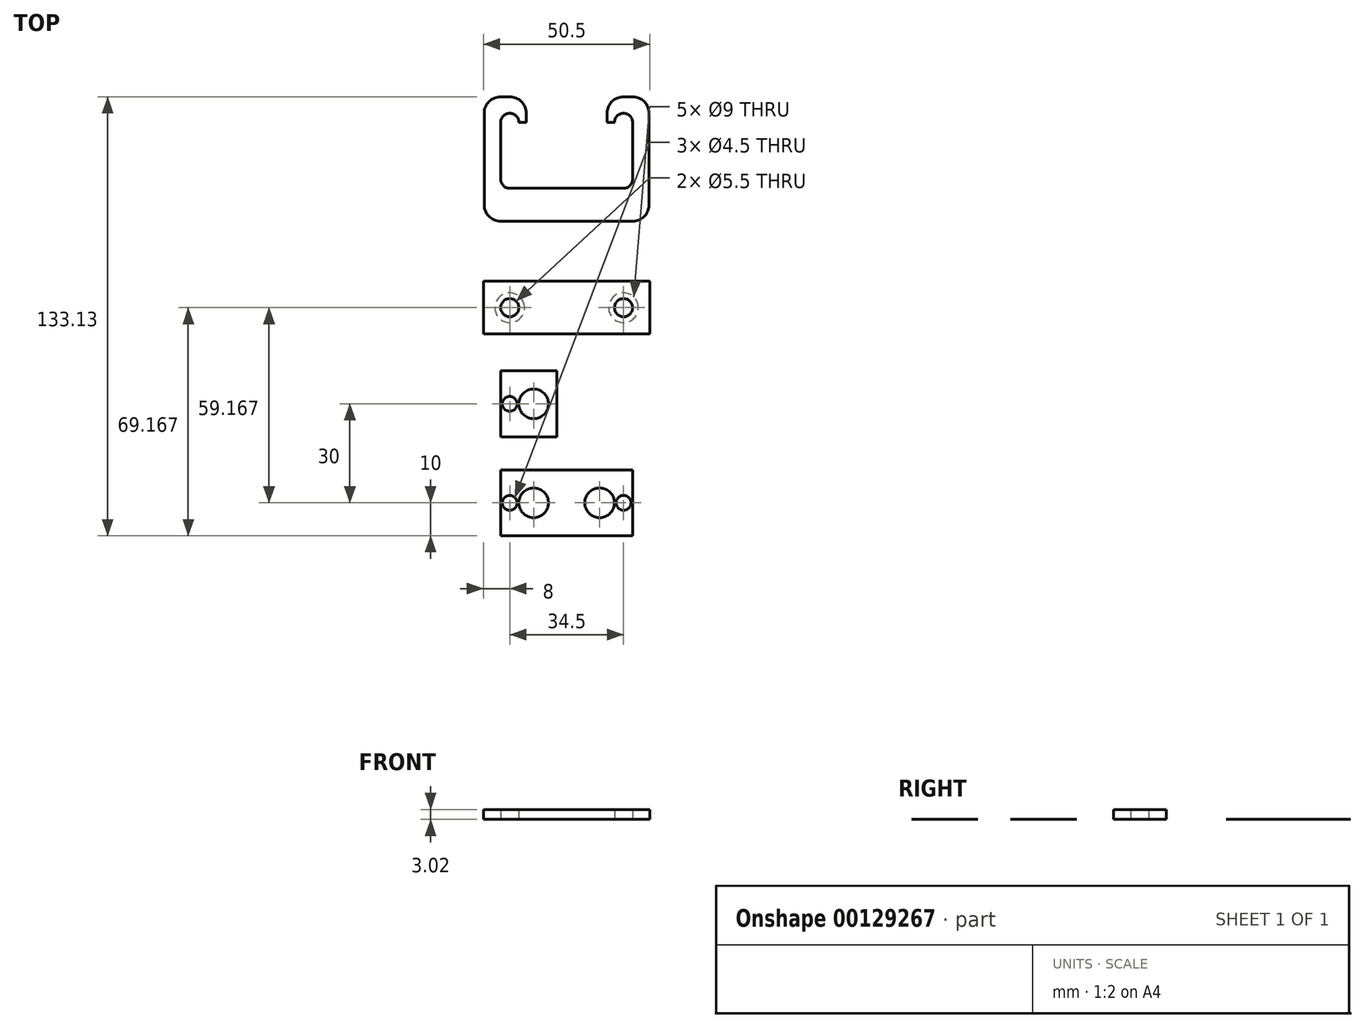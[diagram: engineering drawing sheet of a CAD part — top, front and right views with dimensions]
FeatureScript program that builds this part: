
annotation { "Feature Type Name" : "Feature", "Feature Type Description" : "" }
export const myFeature = defineFeature(function(context is Context, id is Id, definition is map)
    precondition{}
    {
        {
            var Q0;
            Q0=qCreatedBy(makeId("Top.planeOp"),FACE);
            var sketch = newSketch(context, id + "F0", { "sketchPlane" : qUnion([Q0])});
            skLineSegment(sketch, "E0.bottom", {"start": v(20, -10) * mm, "end": v(-20, -10) * mm});
            skLineSegment(sketch, "E0.top", {"start": v(20, 10) * mm, "end": v(-20, 10) * mm});
            skLineSegment(sketch, "E0.left", {"start": v(20, -10) * mm, "end": v(20, 10) * mm});
            skLineSegment(sketch, "E0.right", {"start": v(-20, -10) * mm, "end": v(-20, 10) * mm});
            skPoint(sketch, "E0.middle", {"position": v(0, 0) * mm});
            skPoint(sketch, "E1", {"position": v(-10, 0) * mm});
            skPoint(sketch, "E2", {"position": v(10, 0) * mm});
            skCircle(sketch, "E3", {"center": v(-10, 0) * mm, "radius": 2.75 * mm});
            skCircle(sketch, "E4", {"center": v(-10, 0) * mm, "radius": 4.5 * mm});
            skPoint(sketch, "E5", {"position": v(-17.25, 0) * mm});
            skCircle(sketch, "E6", {"center": v(-17.25, 0) * mm, "radius": 2.25 * mm});
            skPoint(sketch, "E7", {"position": v(-14.5, 0) * mm});
            skLineSegment(sketch, "E8", {"start": v(-14.5, 0) * mm, "end": v(-20, 0) * mm, "construction": true});
            skPoint(sketch, "E9.MirrorP", {"position": v(17.25, 0) * mm});
            skCircle(sketch, "E10.MirrorC", {"center": v(10, 0) * mm, "radius": 4.5 * mm});
            skPoint(sketch, "E11.MirrorP", {"position": v(14.5, 0) * mm});
            skCircle(sketch, "E12.MirrorC", {"center": v(10, 0) * mm, "radius": 2.75 * mm});
            skCircle(sketch, "E13.MirrorC", {"center": v(17.25, 0) * mm, "radius": 2.25 * mm});
            skLineSegment(sketch, "E14.MirrorCS", {"start": v(14.5, 0) * mm, "end": v(20, 0) * mm, "construction": true});
            skLineSegment(sketch, "E15", {"start": v(-3, 10) * mm, "end": v(-3, -10) * mm});
            skLineSegment(sketch, "E16", {"start": v(3, -10) * mm, "end": v(3, 10) * mm});
            skLineSegment(sketch, "E17", {"start": v(0, 10) * mm, "end": v(0, -10) * mm});
            skSolve(sketch);
        }
        {
            var Q0;
            {var subQ0=sQuery(id+"F0.wireOp",EDGE,"E0.right");Q0=makeQuery(id+"F0.imprint","IMPRINT",FACE,{"disambiguationData":[TD([[makeQuery(id+"F0.imprint","IMPRINT",EDGE,{"derivedFrom":subQ0}),-1.0]])]});}
            var Q1;
            {var subQ0=sQuery(id+"F0.wireOp",EDGE,"E15");Q1=makeQuery(id+"F0.imprint","IMPRINT",FACE,{"disambiguationData":[TD([[makeQuery(id+"F0.imprint","IMPRINT",EDGE,{"derivedFrom":subQ0}),1.0]])]});}
            var Q2;
            {var subQ0=sQuery(id+"F0.wireOp",EDGE,"E16");Q2=makeQuery(id+"F0.imprint","IMPRINT",FACE,{"disambiguationData":[TD([[makeQuery(id+"F0.imprint","IMPRINT",EDGE,{"derivedFrom":subQ0}),1.0]])]});}
            var Q3;
            {var subQ1=sQuery(id+"F0.wireOp",EDGE,"E0.left");Q3=makeQuery(id+"F0.imprint","IMPRINT",FACE,{"disambiguationData":[TD([[makeQuery(id+"F0.imprint","IMPRINT",EDGE,{"derivedFrom":subQ1}),1.0]])]});}
            var Q4;
            Q4=makeQuery(id+"F0.imprint","IMPRINT",FACE,{"disambiguationData":[TD([[makeQuery(id+"F0.imprint","IMPRINT",EDGE,{"derivedFrom":sQuery(id+"F0.wireOp",EDGE,"E3")}),-1.0]])]});
            var Q5;
            Q5=makeQuery(id+"F0.imprint","IMPRINT",FACE,{"disambiguationData":[TD([[makeQuery(id+"F0.imprint","IMPRINT",EDGE,{"derivedFrom":sQuery(id+"F0.wireOp",EDGE,"E10.MirrorC")}),-1.0]])]});
            extrude(context, id + "F1", {"entities" : qUnion([Q0, Q1, Q2, Q3, Q4, Q5]), "oppositeDirection" : true, "depth" : 1 / 50.8 * mm});
        }
        {
            var Q0;
            Q0=makeQuery(id+"F0.imprint","IMPRINT",FACE,{"disambiguationData":[TD([[makeQuery(id+"F0.imprint","IMPRINT",EDGE,{"derivedFrom":sQuery(id+"F0.wireOp",EDGE,"E3")}),-1.0]])]});
            var Q1;
            Q1=makeQuery(id+"F0.imprint","IMPRINT",FACE,{"disambiguationData":[TD([[makeQuery(id+"F0.imprint","IMPRINT",EDGE,{"derivedFrom":sQuery(id+"F0.wireOp",EDGE,"E10.MirrorC")}),-1.0]])]});
            extrude(context, id + "F2", {"entities" : qUnion([Q0, Q1]), "operationType" : NewBodyOperationType.REMOVE, "oppositeDirection" : true, "depth" : 6 * mm});
        }
        {
            var Q0;
            Q0=makeQuery(id+"F1.opExtrude","SWEPT_FACE",FACE,{"disambiguationData":[OSD([sQuery(id+"F0.wireOp",EDGE,"E0.bottom")])]});
            var sketch = newSketch(context, id + "F3", { "sketchPlane" : qUnion([Q0])});
            skPoint(sketch, "E18.0", {"position": v(-3, 0) * mm});
            skPoint(sketch, "E19.0", {"position": v(0, 0) * mm});
            skPoint(sketch, "E20.0", {"position": v(3, 0) * mm});
            skLineSegment(sketch, "E21", {"start": v(-3, 0) * mm, "end": v(0, 0) * mm});
            skLineSegment(sketch, "E22", {"start": v(0, 0) * mm, "end": v(3, 0) * mm});
            skLineSegment(sketch, "E23", {"start": v(-3, 0) * mm, "end": v(-3, -3) * mm});
            skLineSegment(sketch, "E24", {"start": v(-3, -3) * mm, "end": v(3, -3) * mm});
            skLineSegment(sketch, "E25", {"start": v(3, -3) * mm, "end": v(3, 0) * mm});
            skSolve(sketch);
        }
        {
            var Q0;
            Q0=makeQuery(id+"F3.imprint","IMPRINT",FACE,{"disambiguationData":[TD([[makeQuery(id+"F3.imprint","IMPRINT",EDGE,{"derivedFrom":sQuery(id+"F3.wireOp",EDGE,"E21")}),1.0]])]});
            var Q1;
            Q1=sQuery(id+"F3.wireOp",EDGE,"E24");
            extrude(context, id + "F4", {"entities" : qUnion([Q0]), "operationType" : NewBodyOperationType.REMOVE, "surfaceEntities" : qUnion([Q1]), "oppositeDirection" : true, "depth" : 25 * mm});
        }
        {
            var Q0;
            Q0=qCreatedBy(makeId("Top.planeOp"),FACE);
            var sketch = newSketch(context, id + "F5", { "sketchPlane" : qUnion([Q0])});
            skLineSegment(sketch, "E26.bottom", {"start": v(-25.25, 21.17) * mm, "end": v(25.25, 21.17) * mm});
            skLineSegment(sketch, "E26.top", {"start": v(-25.25, 37.17) * mm, "end": v(25.25, 37.17) * mm});
            skLineSegment(sketch, "E26.left", {"start": v(-25.25, 21.17) * mm, "end": v(-25.25, 37.17) * mm});
            skLineSegment(sketch, "E26.right", {"start": v(25.25, 21.17) * mm, "end": v(25.25, 37.17) * mm});
            skLineSegment(sketch, "E27", {"start": v(0, 21.17) * mm, "end": v(0, 10.09) * mm, "construction": true});
            skLineSegment(sketch, "E28", {"start": v(-17.25, 0) * mm, "end": v(-17.25, 37.17) * mm, "construction": true});
            skLineSegment(sketch, "E29", {"start": v(17.25, 0) * mm, "end": v(17.25, 37.17) * mm, "construction": true});
            skLineSegment(sketch, "E30", {"start": v(-25.25, 29.17) * mm, "end": v(25.25, 29.17) * mm, "construction": true});
            skPoint(sketch, "E31.0", {"position": v(-3, 10) * mm});
            skPoint(sketch, "E32.0", {"position": v(3, 10) * mm});
            skLineSegment(sketch, "E33", {"start": v(-3, 10) * mm, "end": v(-3, 37.17) * mm, "construction": true});
            skLineSegment(sketch, "E34", {"start": v(3, 37.17) * mm, "end": v(3, 10) * mm, "construction": true});
            skPoint(sketch, "E35", {"position": v(-3, 21.17) * mm});
            skPoint(sketch, "E36", {"position": v(3, 21.17) * mm});
            skPoint(sketch, "E37", {"position": v(-17.25, 29.17) * mm});
            skPoint(sketch, "E38", {"position": v(17.25, 29.17) * mm});
            skSolve(sketch);
        }
        {
            var Q0;
            Q0 = qSketchRegion(id + "F5", true);
            var Q1;
            Q1=makeQuery(id+"F5.imprint","IMPRINT",FACE,{"disambiguationData":[TD([[makeQuery(id+"F5.imprint","IMPRINT",EDGE,{"derivedFrom":sQuery(id+"F5.wireOp",EDGE,"ofzVHqzz-uNpf-kPzX-PyAA-OWdwubVH7mjJ")}),-1.0]])]});
            var Q2;
            Q2=makeQuery(id+"F5.imprint","IMPRINT",FACE,{"disambiguationData":[TD([[makeQuery(id+"F5.imprint","IMPRINT",EDGE,{"derivedFrom":sQuery(id+"F5.wireOp",EDGE,"o32WaDat-DvT3-jpnh-iwgM-FfQ55ZiCaMmG")}),-1.0]])]});
            extrude(context, id + "F6", {"entities" : qUnion([Q0, Q1, Q2]), "oppositeDirection" : true, "depth" : 1 / 50.8 * mm});
        }
        {
            var Q0;
            Q0=sQuery(id+"F5.wireOp",VERTEX,"E37");
            var Q1;
            Q1=sQuery(id+"F5.wireOp",VERTEX,"E38");
            var Q2;
            Q2=makeQuery(id+"F6.opExtrude","SWEPT_BODY",BODY,{"disambiguationData":[OSD([sQuery(id+"F5.wireOp",EDGE,"E26.bottom"),sQuery(id+"F5.wireOp",EDGE,"E26.top"),sQuery(id+"F5.wireOp",EDGE,"E26.left"),sQuery(id+"F5.wireOp",EDGE,"E26.right")])]});
            hole(context, id + "F7", {"style" : HoleStyle.C_BORE, "endStyle" : HoleEndStyle.THROUGH, "holeDiameter" : 5.5 * mm, "cBoreDiameter" : 9 * mm, "cBoreDepth" : 5 * mm, "startFromSketch" : true, "locations" : qUnion([Q0, Q1]), "scope" : qUnion([Q2]), "isTappedThrough" : true});
        }
        {
            var Q0;
            Q0=qCreatedBy(makeId("Top.planeOp"),FACE);
            var sketch = newSketch(context, id + "F8", { "sketchPlane" : qUnion([Q0])});
            skLineSegment(sketch, "E39.bottom", {"start": v(25, 55.38) * mm, "end": v(-25, 55.38) * mm});
            skLineSegment(sketch, "E39.top", {"start": v(25, 80.88) * mm, "end": v(-25, 80.88) * mm, "construction": true});
            skLineSegment(sketch, "E39.left", {"start": v(25, 55.38) * mm, "end": v(25, 80.88) * mm});
            skLineSegment(sketch, "E39.right", {"start": v(-25, 55.38) * mm, "end": v(-25, 80.88) * mm});
            skPoint(sketch, "E39.middle", {"position": v(0, 68.13) * mm});
            skPoint(sketch, "E40.0", {"position": v(25.25, 37.17) * mm});
            skPoint(sketch, "E41.0", {"position": v(17.25, 37.17) * mm});
            skPoint(sketch, "E42.0", {"position": v(-17.25, 37.17) * mm});
            skLineSegment(sketch, "E43", {"start": v(17.25, 37.17) * mm, "end": v(17.25, 93.13) * mm, "construction": true});
            skLineSegment(sketch, "E44", {"start": v(-17.25, 37.17) * mm, "end": v(-17.25, 93.13) * mm, "construction": true});
            skLineSegment(sketch, "E45", {"start": v(-25, 68.13) * mm, "end": v(25, 68.13) * mm, "construction": true});
            skPoint(sketch, "E46", {"position": v(-17.25, 68.13) * mm});
            skPoint(sketch, "E47", {"position": v(17.25, 68.13) * mm});
            skCircle(sketch, "E48", {"center": v(-17.25, 68.13) * mm, "radius": 2.75 * mm});
            skCircle(sketch, "E49", {"center": v(17.25, 68.13) * mm, "radius": 2.75 * mm});
            skLineSegment(sketch, "E50", {"start": v(-25, 93.13) * mm, "end": v(-12.25, 93.13) * mm});
            skLineSegment(sketch, "E51", {"start": v(-25, 93.13) * mm, "end": v(-25, 80.88) * mm});
            skLineSegment(sketch, "E52", {"start": v(25, 93.13) * mm, "end": v(25, 80.88) * mm});
            skLineSegment(sketch, "E53", {"start": v(-20, 68.13) * mm, "end": v(-20, 85.38) * mm});
            skLineSegment(sketch, "E54", {"start": v(20, 68.13) * mm, "end": v(20, 85.38) * mm});
            skLineSegment(sketch, "E55", {"start": v(17.25, 65.38) * mm, "end": v(-17.25, 65.38) * mm});
            skPoint(sketch, "E56", {"position": v(17.25, 55.38) * mm});
            skPoint(sketch, "E57", {"position": v(-17.25, 85.38) * mm});
            skPoint(sketch, "E58", {"position": v(17.25, 85.38) * mm});
            skCircle(sketch, "E59", {"center": v(-17.25, 85.38) * mm, "radius": 2.75 * mm});
            skCircle(sketch, "E60", {"center": v(17.25, 85.38) * mm, "radius": 2.75 * mm});
            skLineSegment(sketch, "E61", {"start": v(-17.25, 85.38) * mm, "end": v(-14.5, 85.38) * mm, "construction": true});
            skLineSegment(sketch, "E62", {"start": v(-12.25, 85.38) * mm, "end": v(-12.25, 93.13) * mm});
            skLineSegment(sketch, "E63", {"start": v(12.25, 85.38) * mm, "end": v(12.25, 93.13) * mm});
            skLineSegment(sketch, "E64", {"start": v(-12.25, 85.38) * mm, "end": v(12.25, 85.38) * mm, "construction": true});
            skLineSegment(sketch, "E65", {"start": v(12.25, 85.38) * mm, "end": v(14.5, 85.38) * mm});
            skLineSegment(sketch, "E66", {"start": v(12.25, 93.13) * mm, "end": v(25, 93.13) * mm});
            skLineSegment(sketch, "E67", {"start": v(-12.25, 93.13) * mm, "end": v(12.25, 93.13) * mm, "construction": true});
            skLineSegment(sketch, "E68", {"start": v(-20, 85.38) * mm, "end": v(-20, 93.13) * mm, "construction": true});
            skLineSegment(sketch, "E69", {"start": v(20, 85.38) * mm, "end": v(20, 93.13) * mm, "construction": true});
            skLineSegment(sketch, "E70", {"start": v(-14.5, 85.38) * mm, "end": v(-12.25, 85.38) * mm});
            skLineSegment(sketch, "E71", {"start": v(14.5, 85.38) * mm, "end": v(17.25, 85.38) * mm, "construction": true});
            skPoint(sketch, "E72", {"position": v(17.25, 88.13) * mm});
            skSolve(sketch);
        }
        {
            var Q0;
            Q0=makeQuery(id+"F8.imprint","IMPRINT",FACE,{"disambiguationData":[TD([[makeQuery(id+"F8.imprint","IMPRINT",EDGE,{"derivedFrom":sQuery(id+"F8.wireOp",EDGE,"E39.bottom")}),-1.0]])]});
            extrude(context, id + "F9", {"entities" : qUnion([Q0]), "depth" : 1 / 50.8 * mm});
        }
        {
            var Q0;
            Q0=makeQuery(id+"F9.opExtrude","SWEPT_EDGE",EDGE,{"disambiguationData":[OSD([sQuery(id+"F8.wireOp",EDGE,"E50"),sQuery(id+"F8.wireOp",EDGE,"E51")])]});
            var Q1;
            Q1=makeQuery(id+"F9.opExtrude","SWEPT_EDGE",EDGE,{"disambiguationData":[OSD([sQuery(id+"F8.wireOp",EDGE,"E52"),sQuery(id+"F8.wireOp",EDGE,"E66")])]});
            var Q2;
            Q2=makeQuery(id+"F9.opExtrude","SWEPT_EDGE",EDGE,{"disambiguationData":[OSD([sQuery(id+"F8.wireOp",EDGE,"E39.bottom"),sQuery(id+"F8.wireOp",EDGE,"E39.left")])]});
            var Q3;
            Q3=makeQuery(id+"F9.opExtrude","SWEPT_EDGE",EDGE,{"disambiguationData":[OSD([sQuery(id+"F8.wireOp",EDGE,"E39.bottom"),sQuery(id+"F8.wireOp",EDGE,"E39.right")])]});
            fillet(context, id + "F10", {"entities" : qUnion([Q0, Q1, Q2, Q3]), "radius" : 5 * mm, "tangentPropagation" : true, "allowEdgeOverflow" : false});
        }
        {
            var Q0;
            Q0=makeQuery(id+"F9.opExtrude","SWEPT_EDGE",EDGE,{"disambiguationData":[OSD([sQuery(id+"F8.wireOp",EDGE,"E50"),sQuery(id+"F8.wireOp",EDGE,"E62")])]});
            var Q1;
            Q1=makeQuery(id+"F9.opExtrude","SWEPT_EDGE",EDGE,{"disambiguationData":[OSD([sQuery(id+"F8.wireOp",EDGE,"E63"),sQuery(id+"F8.wireOp",EDGE,"E66")])]});
            fillet(context, id + "F11", {"entities" : qUnion([Q0, Q1]), "radius" : 5 * mm, "tangentPropagation" : true, "allowEdgeOverflow" : false});
        }
        {
            var Q0;
            Q0=qCreatedBy(makeId("Top.planeOp"),FACE);
            var sketch = newSketch(context, id + "F12", { "sketchPlane" : qUnion([Q0])});
            skLineSegment(sketch, "E73.bottom", {"start": v(20, -20) * mm, "end": v(-20, -20) * mm});
            skLineSegment(sketch, "E73.top", {"start": v(20, -40) * mm, "end": v(-20, -40) * mm});
            skLineSegment(sketch, "E73.left", {"start": v(20, -20) * mm, "end": v(20, -40) * mm});
            skLineSegment(sketch, "E73.right", {"start": v(-20, -20) * mm, "end": v(-20, -40) * mm});
            skPoint(sketch, "E73.middle", {"position": v(0, -30) * mm});
            skLineSegment(sketch, "E74", {"start": v(-20, -30) * mm, "end": v(20, -30) * mm, "construction": true});
            skPoint(sketch, "E75.0", {"position": v(-20, -10) * mm});
            skPoint(sketch, "E76.0", {"position": v(-17.25, 0) * mm});
            skPoint(sketch, "E77.0", {"position": v(-10, 0) * mm});
            skPoint(sketch, "E78.0", {"position": v(10, 0) * mm});
            skPoint(sketch, "E79.0", {"position": v(17.25, 0) * mm});
            skPoint(sketch, "E80.0", {"position": v(20, -10) * mm});
            skLineSegment(sketch, "E81", {"start": v(-20, -10) * mm, "end": v(-20, -20) * mm, "construction": true});
            skLineSegment(sketch, "E82", {"start": v(20, -10) * mm, "end": v(20, -20) * mm, "construction": true});
            skLineSegment(sketch, "E83", {"start": v(-17.25, 0) * mm, "end": v(-17.25, -30) * mm, "construction": true});
            skLineSegment(sketch, "E84", {"start": v(-10, 0) * mm, "end": v(-10, -30) * mm, "construction": true});
            skLineSegment(sketch, "E85", {"start": v(10, -30) * mm, "end": v(10, 0) * mm, "construction": true});
            skLineSegment(sketch, "E86", {"start": v(17.25, 0) * mm, "end": v(17.25, -30) * mm, "construction": true});
            skPoint(sketch, "E87.0", {"position": v(-20, 10) * mm});
            skLineSegment(sketch, "E88", {"start": v(-20, 10) * mm, "end": v(-20, -10) * mm, "construction": true});
            skSolve(sketch);
        }
        {
            var Q0;
            Q0=makeQuery(id+"F12.imprint","IMPRINT",FACE,{"disambiguationData":[TD([[makeQuery(id+"F12.imprint","IMPRINT",EDGE,{"derivedFrom":sQuery(id+"F12.wireOp",EDGE,"E73.bottom")}),1.0]])]});
            var Q1;
            Q1=sQuery(id+"F12.wireOp",EDGE,"E74");
            extrude(context, id + "F13", {"entities" : qUnion([Q0]), "surfaceEntities" : qUnion([Q1]), "oppositeDirection" : true, "depth" : 1 / 50.8 * mm});
        }
        {
            var Q0;
            Q0=sQuery(id+"F12.wireOp",VERTEX,"E83.end");
            var Q1;
            Q1=sQuery(id+"F12.wireOp",VERTEX,"E86.end");
            var Q2;
            Q2=makeQuery(id+"F13.opExtrude","SWEPT_BODY",BODY,{"disambiguationData":[OSD([sQuery(id+"F12.wireOp",EDGE,"E73.bottom"),sQuery(id+"F12.wireOp",EDGE,"E73.top"),sQuery(id+"F12.wireOp",EDGE,"E73.left"),sQuery(id+"F12.wireOp",EDGE,"E73.right")])]});
            hole(context, id + "F14", {"style" : HoleStyle.SIMPLE, "endStyle" : HoleEndStyle.THROUGH, "holeDiameter" : 4.5 * mm, "startFromSketch" : true, "locations" : qUnion([Q0, Q1]), "scope" : qUnion([Q2]), "isTappedThrough" : true});
        }
        {
            var Q0;
            Q0=sQuery(id+"F12.wireOp",VERTEX,"E84.end");
            var Q1;
            Q1=sQuery(id+"F12.wireOp",VERTEX,"E85.start");
            var Q2;
            Q2=makeQuery(id+"F13.opExtrude","SWEPT_BODY",BODY,{"disambiguationData":[OSD([sQuery(id+"F12.wireOp",EDGE,"E73.bottom"),sQuery(id+"F12.wireOp",EDGE,"E73.top"),sQuery(id+"F12.wireOp",EDGE,"E73.left"),sQuery(id+"F12.wireOp",EDGE,"E73.right")])]});
            hole(context, id + "F15", {"style" : HoleStyle.C_BORE, "endStyle" : HoleEndStyle.THROUGH, "holeDiameter" : 5.5 * mm, "cBoreDiameter" : 9 * mm, "cBoreDepth" : 6 * mm, "startFromSketch" : true, "locations" : qUnion([Q0, Q1]), "scope" : qUnion([Q2]), "isTappedThrough" : true});
        }
        {
            var Q0;
            Q0=makeQuery(id+"F13.opExtrude","SWEPT_FACE",FACE,{"disambiguationData":[OSD([sQuery(id+"F12.wireOp",EDGE,"E73.top")])]});
            var sketch = newSketch(context, id + "F16", { "sketchPlane" : qUnion([Q0])});
            skPoint(sketch, "E89.0", {"position": v(-20, 0) * mm});
            skPoint(sketch, "E90.0", {"position": v(20, 0) * mm});
            skLineSegment(sketch, "E91", {"start": v(0, -4) * mm, "end": v(-4, 0) * mm});
            skLineSegment(sketch, "E92", {"start": v(0, -4) * mm, "end": v(4, 0) * mm});
            skLineSegment(sketch, "E93", {"start": v(-20, 0) * mm, "end": v(20, 0) * mm, "construction": true});
            skLineSegment(sketch, "E94", {"start": v(20, -12.7) * mm, "end": v(-20, -12.7) * mm, "construction": true});
            skLineSegment(sketch, "E95", {"start": v(0, 0) * mm, "end": v(0, -12.7) * mm, "construction": true});
            skLineSegment(sketch, "E96", {"start": v(-4, 0) * mm, "end": v(4, 0) * mm});
            skSolve(sketch);
        }
        {
            var Q0;
            Q0=makeQuery(id+"F16.imprint","IMPRINT",FACE,{"disambiguationData":[TD([[makeQuery(id+"F16.imprint","IMPRINT",EDGE,{"derivedFrom":sQuery(id+"F16.wireOp",EDGE,"E91")}),-1.0]])]});
            extrude(context, id + "F17", {"entities" : qUnion([Q0]), "operationType" : NewBodyOperationType.REMOVE, "endBound" : BoundingType.THROUGH_ALL, "oppositeDirection" : true, "depth" : 25 * mm});
        }
        {
            var Q0;
            Q0=makeQuery(id+"F5.imprint","IMPRINT",FACE,{"disambiguationData":[TD([[makeQuery(id+"F5.imprint","IMPRINT",EDGE,{"derivedFrom":sQuery(id+"F5.wireOp",EDGE,"E26.bottom")}),1.0]])]});
            extrude(context, id + "F18", {"entities" : qUnion([Q0]), "depth" : 3 * mm});
        }
        {
            var Q0;
            Q0=sQuery(id+"F5.wireOp",VERTEX,"E37");
            var Q1;
            Q1=sQuery(id+"F5.wireOp",VERTEX,"E38");
            var Q2;
            Q2=makeQuery(id+"F18.opExtrude","SWEPT_BODY",BODY,{"disambiguationData":[OSD([sQuery(id+"F5.wireOp",EDGE,"E26.bottom"),sQuery(id+"F5.wireOp",EDGE,"E26.top"),sQuery(id+"F5.wireOp",EDGE,"E26.left"),sQuery(id+"F5.wireOp",EDGE,"E26.right")])]});
            hole(context, id + "F19", {"style" : HoleStyle.SIMPLE, "endStyle" : HoleEndStyle.THROUGH, "oppositeDirection" : true, "holeDiameter" : 5.5 * mm, "startFromSketch" : true, "locations" : qUnion([Q0, Q1]), "scope" : qUnion([Q2]), "isTappedThrough" : true});
        }
    });
